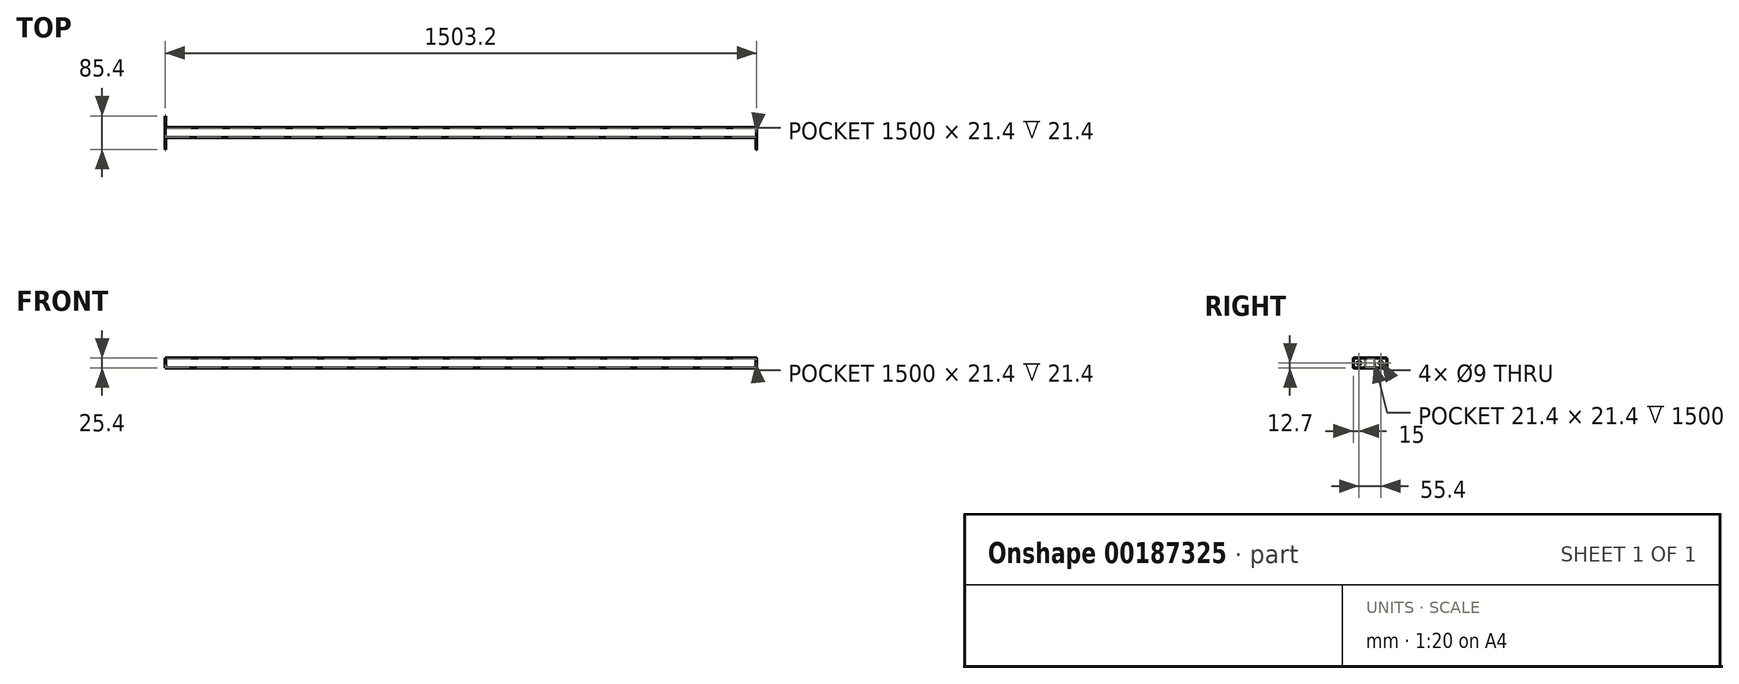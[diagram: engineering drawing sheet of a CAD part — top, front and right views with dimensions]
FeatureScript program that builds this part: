
annotation { "Feature Type Name" : "Feature", "Feature Type Description" : "" }
export const myFeature = defineFeature(function(context is Context, id is Id, definition is map)
    precondition{}
    {
        {
            var Q0;
            Q0=qCreatedBy(makeId("Right.planeOp"),FACE);
            var sketch = newSketch(context, id + "F0", { "sketchPlane" : qUnion([Q0])});
            skLineSegment(sketch, "E0.bottom", {"start": v(12.7, -12.7) * mm, "end": v(-12.7, -12.7) * mm});
            skLineSegment(sketch, "E0.top", {"start": v(12.7, 12.7) * mm, "end": v(-12.7, 12.7) * mm});
            skLineSegment(sketch, "E0.left", {"start": v(12.7, -12.7) * mm, "end": v(12.7, 12.7) * mm});
            skLineSegment(sketch, "E0.right", {"start": v(-12.7, -12.7) * mm, "end": v(-12.7, 12.7) * mm});
            skPoint(sketch, "E0.middle", {"position": v(0, 0) * mm});
            skSolve(sketch);
        }
        {
            var Q0;
            Q0=qSketchRegion(id+"F0",true);
            extrude(context, id + "F1", {"entities" : qUnion([Q0]), "endBound" : BoundingType.SYMMETRIC, "depth" : 1500 * mm});
        }
        {
            var Q0;
            Q0=makeQuery(id+"F1.opExtrude","CAP_FACE",FACE,{"disambiguationData":[OSD([sQuery(id+"F0.wireOp",EDGE,"E0.bottom"),sQuery(id+"F0.wireOp",EDGE,"E0.top"),sQuery(id+"F0.wireOp",EDGE,"E0.left"),sQuery(id+"F0.wireOp",EDGE,"E0.right")])],"isStart":false});
            var Q1;
            Q1=makeQuery(id+"F1.opExtrude","CAP_FACE",FACE,{"disambiguationData":[OSD([sQuery(id+"F0.wireOp",EDGE,"E0.bottom"),sQuery(id+"F0.wireOp",EDGE,"E0.top"),sQuery(id+"F0.wireOp",EDGE,"E0.left"),sQuery(id+"F0.wireOp",EDGE,"E0.right")])],"isStart":true});
            shell(context, id + "F2", {"entities" : qUnion([Q0, Q1]), "thickness" : 2 * mm});
        }
        {
            var Q0;
            Q0=makeQuery(id+"F1.opExtrude","CAP_FACE",FACE,{"disambiguationData":[OSD([sQuery(id+"F0.wireOp",EDGE,"E0.bottom"),sQuery(id+"F0.wireOp",EDGE,"E0.top"),sQuery(id+"F0.wireOp",EDGE,"E0.left"),sQuery(id+"F0.wireOp",EDGE,"E0.right")])],"isStart":false});
            var sketch = newSketch(context, id + "F3", { "sketchPlane" : qUnion([Q0])});
            skLineSegment(sketch, "E1.0", {"start": v(40.7, 12.7) * mm, "end": v(-40.7, 12.7) * mm});
            skLineSegment(sketch, "E2.0", {"start": v(40.7, -12.7) * mm, "end": v(-40.7, -12.7) * mm});
            skLineSegment(sketch, "E3.0", {"start": v(42.7, -10.7) * mm, "end": v(42.7, 10.7) * mm});
            skLineSegment(sketch, "E4.0", {"start": v(-42.7, -10.7) * mm, "end": v(-42.7, 10.7) * mm});
            skPoint(sketch, "E5.0.end.orphan", {"position": v(-12.7, 12.7) * mm});
            skPoint(sketch, "E5.0.start.orphan", {"position": v(-12.7, -12.7) * mm});
            skPoint(sketch, "E6.0.end.orphan", {"position": v(12.7, 12.7) * mm});
            skPoint(sketch, "E6.0.start.orphan", {"position": v(12.7, -12.7) * mm});
            skPoint(sketch, "E7.visualSharp", {"position": v(-42.7, 12.7) * mm});
            skArc(sketch, "E7.filletArc", {"start": v(-40.7, 12.7) * mm, "mid": v(-42.11, 12.11) * mm, "end": v(-42.7, 10.7) * mm});
            skPoint(sketch, "E8.visualSharp", {"position": v(-42.7, -12.7) * mm});
            skArc(sketch, "E8.filletArc", {"start": v(-42.7, -10.7) * mm, "mid": v(-42.11, -12.11) * mm, "end": v(-40.7, -12.7) * mm});
            skPoint(sketch, "E9.visualSharp", {"position": v(42.7, -12.7) * mm});
            skArc(sketch, "E9.filletArc", {"start": v(40.7, -12.7) * mm, "mid": v(42.11, -12.11) * mm, "end": v(42.7, -10.7) * mm});
            skPoint(sketch, "E10.visualSharp", {"position": v(42.7, 12.7) * mm});
            skArc(sketch, "E10.filletArc", {"start": v(42.7, 10.7) * mm, "mid": v(42.11, 12.11) * mm, "end": v(40.7, 12.7) * mm});
            skCircle(sketch, "E11", {"center": v(-27.7, 0) * mm, "radius": 4.5 * mm});
            skCircle(sketch, "E12", {"center": v(27.7, 0) * mm, "radius": 4.5 * mm});
            skSolve(sketch);
        }
        {
            var Q0;
            Q0=qSketchRegion(id+"F3",true);
            extrude(context, id + "F4", {"entities" : qUnion([Q0]), "operationType" : NewBodyOperationType.ADD, "depth" : 1.6 * mm});
        }
        {
            var Q0;
            Q0=makeQuery(id+"F1.opExtrude","CAP_FACE",FACE,{"disambiguationData":[OSD([sQuery(id+"F0.wireOp",EDGE,"E0.bottom"),sQuery(id+"F0.wireOp",EDGE,"E0.top"),sQuery(id+"F0.wireOp",EDGE,"E0.left"),sQuery(id+"F0.wireOp",EDGE,"E0.right")])],"isStart":true});
            var sketch = newSketch(context, id + "F5", { "sketchPlane" : qUnion([Q0])});
            skLineSegment(sketch, "E13.0", {"start": v(-40.7, 12.7) * mm, "end": v(-12.7, 12.7) * mm});
            skArc(sketch, "E13.1", {"start": v(-42.7, 10.7) * mm, "mid": v(-42.11, 12.11) * mm, "end": v(-40.7, 12.7) * mm});
            skLineSegment(sketch, "E13.2.0", {"start": v(-40.7, -12.7) * mm, "end": v(-12.7, -12.7) * mm});
            skLineSegment(sketch, "E13.2.1", {"start": v(-12.7, -12.7) * mm, "end": v(-12.7, 12.7) * mm});
            skLineSegment(sketch, "E13.2.2", {"start": v(-12.7, 12.7) * mm, "end": v(-40.7, 12.7) * mm});
            skArc(sketch, "E13.2.3", {"start": v(-40.7, 12.7) * mm, "mid": v(-42.11, 12.11) * mm, "end": v(-42.7, 10.7) * mm});
            skLineSegment(sketch, "E13.2.4", {"start": v(-42.7, 10.7) * mm, "end": v(-42.7, -10.7) * mm});
            skArc(sketch, "E13.2.5", {"start": v(-42.7, -10.7) * mm, "mid": v(-42.11, -12.11) * mm, "end": v(-40.7, -12.7) * mm});
            skLineSegment(sketch, "E13.3", {"start": v(-12.7, -12.7) * mm, "end": v(12.7, -12.7) * mm});
            skLineSegment(sketch, "E13.4", {"start": v(12.7, -12.7) * mm, "end": v(40.7, -12.7) * mm});
            skArc(sketch, "E13.5", {"start": v(42.7, -10.7) * mm, "mid": v(42.11, -12.11) * mm, "end": v(40.7, -12.7) * mm});
            skLineSegment(sketch, "E13.6", {"start": v(42.7, -10.7) * mm, "end": v(42.7, 10.7) * mm});
            skArc(sketch, "E13.7", {"start": v(40.7, 12.7) * mm, "mid": v(42.11, 12.11) * mm, "end": v(42.7, 10.7) * mm});
            skLineSegment(sketch, "E13.8", {"start": v(12.7, 12.7) * mm, "end": v(40.7, 12.7) * mm});
            skLineSegment(sketch, "E13.9", {"start": v(-12.7, 12.7) * mm, "end": v(12.7, 12.7) * mm});
            skCircle(sketch, "E13.10", {"center": v(27.7, 0) * mm, "radius": 4.5 * mm});
            skCircle(sketch, "E14.0", {"center": v(-27.7, 0) * mm, "radius": 4.5 * mm});
            skSolve(sketch);
        }
        {
            var Q0;
            Q0=qSketchRegion(id+"F5",true);
            extrude(context, id + "F6", {"entities" : qUnion([Q0]), "operationType" : NewBodyOperationType.ADD, "depth" : 1.6 * mm});
        }
    });
